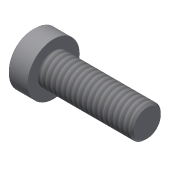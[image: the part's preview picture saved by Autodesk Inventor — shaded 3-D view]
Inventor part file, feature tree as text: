
AUTODESK INVENTOR PART (.ipt)
format: ipt  version: 2022.5 (Build 265521000, 521)  size: 115,712 bytes
history: native  units: in
note: dims shown in document units (in); Inventor stores cm internally (conversion verified against a paired STEP export)
features: chamfer x2, revolve x1, thread x1, extrude x1, sketch x1
ambient origin geometry x8: Origin, YZ Plane, XZ Plane, XY Plane, X Axis, Y Axis, Z Axis, Center Point
bodies: Solid1 (feature_tree)
feature tree (6):
  revolve  "Revolution1"  [1 undecoded]
  chamfer  "Chamfer5"  Distance=0.0984in
  thread  "Thread8"  [1 undecoded]
  extrude  "Extrusion19"  Depth=0.0787in
  chamfer  "Chamfer6"  Distance=0.3543in
  sketch  "Sketch20"  dims[d21=0.7874in d84=0.0591in d87=0.0984in d92=90.0deg d116=0.0787in d117=0.3543in d118=0.0079in d119=0.0787in d120=45.0deg d141=0.3937in d142=0.0in d143=0.0984in d144=0.0591in d145=0.0in d146=0.0079in d147=0.0787in d148=45.0deg]
note: 2 required parameter values undecoded (feature->parameter linkage not recoverable at this tier; creation-order binding heuristic only, values carry confidence <= 0.55)